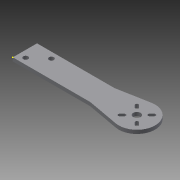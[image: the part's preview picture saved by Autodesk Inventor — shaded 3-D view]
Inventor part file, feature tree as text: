
AUTODESK INVENTOR PART (.ipt)
format: ipt  version: 2015 (Build 190159000, 159)  size: 145,920 bytes
history: native  units: mm
features: sketch x9, extrude x7, pattern_circular x1, fillet x1
ambient origin geometry x8: Origin, YZ Plane, XZ Plane, XY Plane, X Axis, Y Axis, Z Axis, Center Point
bodies: Solid1 (feature_tree)
feature tree (18):
  sketch  "Sketch1"  dims[d5=30.0mm d6=92.5mm]
  extrude  "Extrusion1"  Depth=92.5mm
  extrude  "Extrusion2"  Depth=3.0mm
  extrude  "Extrusion3"  Depth=2.6mm
  pattern_circular  "Circular Pattern1"  Count=4 Angle=360.0deg
  extrude  "Extrusion4"  Depth=20.0mm
  extrude  "Extrusion5"  Depth=10.0mm TaperAngle=0.0deg
  extrude  "Extrusion6"  Depth=4.064mm
  sketch  "Sketch7"  dims[d26=20.0mm d27=3.2mm]
  sketch  "Sketch8"  dims[d28=3.2mm d29=10.0mm d30=0.0mm]
  sketch  "Sketch9"  dims[d31=4.064mm d32=4.064mm]
  extrude  "Extrusion7"  Depth=2.0mm
  fillet  "Fillet1"  Radius=10.0mm
  sketch  "Sketch3"  dims[d7=3.0mm d8=0.0mm d9=3.0mm]
  sketch  "Sketch4"  dims[d10=10.0mm d11=0.0mm d18=2.6mm]
  sketch  "Sketch5"  dims[d19=2.6mm]
  sketch  "Sketch6"  dims[d21=10.0mm d22=0.0mm d23=40.0mm d24=360.0deg]
  sketch  "Sketch10"  dims[d33=10.0mm d34=0.0mm d35=6.1468mm d36=10.0mm d37=0.0mm d38=22.5mm d39=2.0mm d40=0.0mm d41=2.0mm]
